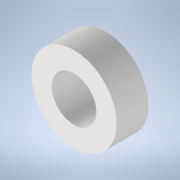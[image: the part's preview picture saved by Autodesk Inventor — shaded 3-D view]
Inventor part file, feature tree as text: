
AUTODESK INVENTOR PART (.ipt)
format: ipt  version: 2020 (Build 240168000, 168)  size: 194,048 bytes
history: native  units: mm
features: sketch x5, plane x4, extrude x3, other x3, revolve x1, reference x1, projected_geometry x1
ambient origin geometry x8: Origin, YZ Plane, XZ Plane, XY Plane, X Axis, Y Axis, Z Axis, Center Point
bodies: Volumenkörper1 (feature_tree)
feature tree (18):
  extrude  "Extrusion1"  Depth=4.0mm TaperAngle=0.0deg
  sketch  "Skizze2"  dims[d6=3.0mm d8=8.5mm]
  plane  "Arbeitsebene2"
  revolve  "Umdrehung2"
  extrude  "Extrusion3"  Depth=8.5mm
  sketch  "Skizze7"  dims[d12=5.0mm]
  plane  "Arbeitsebene4"
  extrude  "Extrusion4"  Depth=7.247mm TaperAngle=0.0deg
  sketch  "Skizze1"  dims[d0=4.0mm d1=1.5mm d2=0.0mm]
  reference  "Referenz1"
  plane  "Arbeitsebene1"
  sketch  "Skizze5"  dims[d9=90.0deg d10=7.247mm d11=0.0mm]
  projected_geometry  "Projizierte Kontur1"
  plane  "Arbeitsebene3"
  sketch  "Skizze8"  dims[d13=4.0mm d14=0.0mm]
  parser-record x1  (decoder bookkeeping rows leaked as tree rows — omitted from the tree; the rows remain in map.json)
  other  "GlassesAssembly.iam"
  other  "CameraArm:1"
note: 1 file-system path scrubbed to <path> (originals preserved in map.json)
